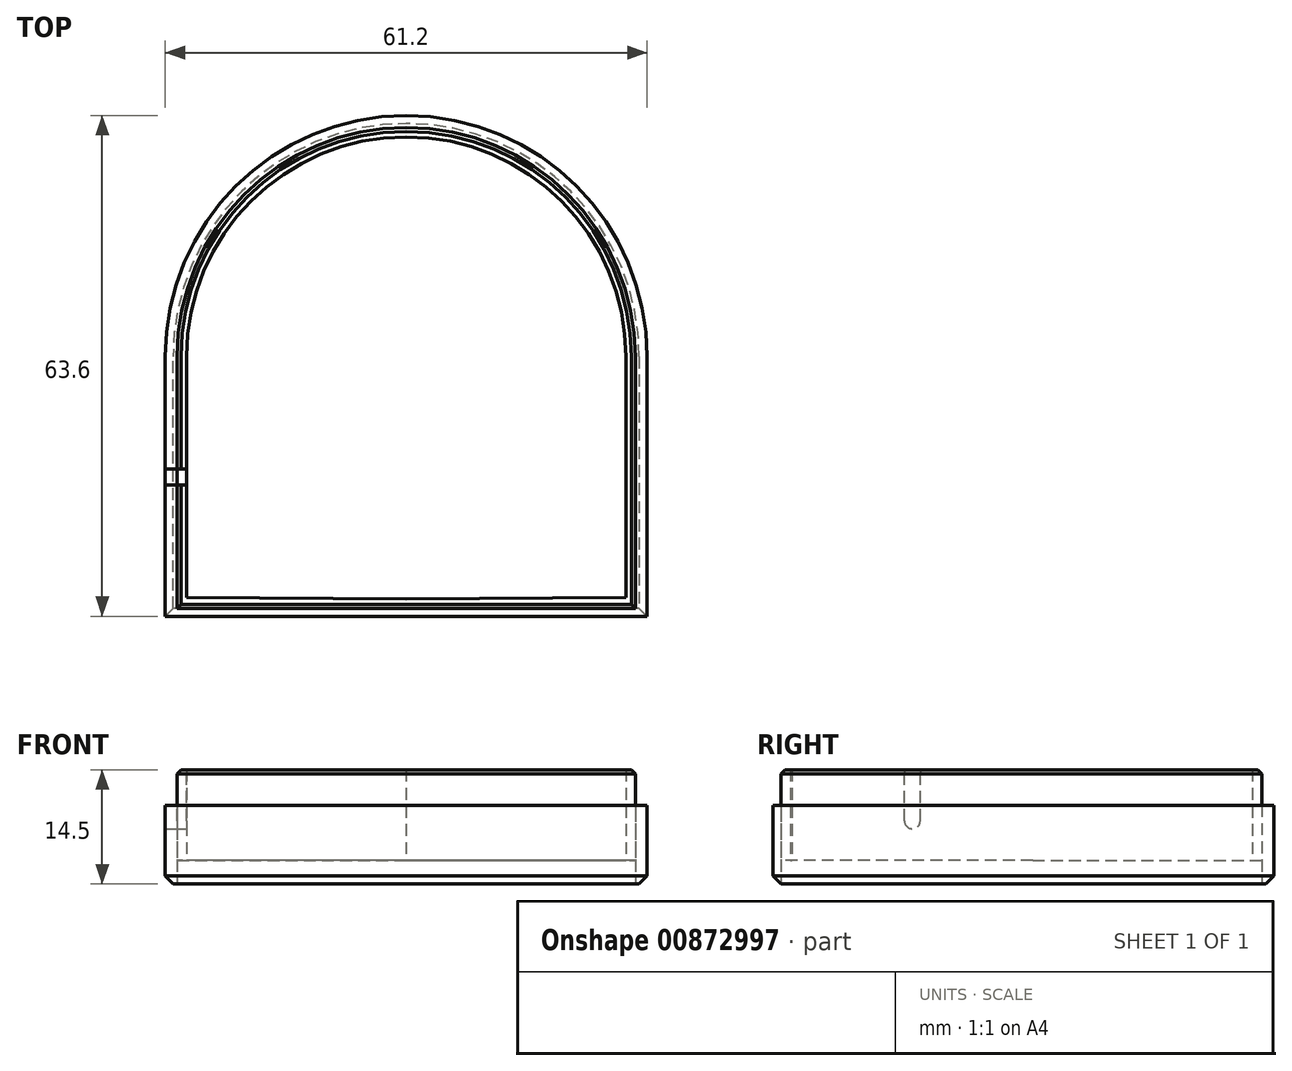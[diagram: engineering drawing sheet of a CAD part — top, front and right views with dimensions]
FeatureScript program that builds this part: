
annotation { "Feature Type Name" : "Feature", "Feature Type Description" : "" }
export const myFeature = defineFeature(function(context is Context, id is Id, definition is map)
    precondition{}
    {
        {
            assignVariable(context, id + "F0", {"name" : "LongExt", "anyValue" : 10});
        }
        {
            assignVariable(context, id + "F1", {"name" : "Renfoncement", "anyValue" : 1.5});
        }
        {
            var Q0;
            Q0=qCreatedBy(makeId("Top.planeOp"),FACE);
            var sketch = newSketch(context, id + "F2", { "sketchPlane" : qUnion([Q0])});
            skCircle(sketch, "E0", {"center": v(0, 0) * mm, "radius": 29.1 * mm});
            skCircle(sketch, "E1", {"center": v(0, 0) * mm, "radius": 30.6 * mm});
            skLineSegment(sketch, "E2", {"start": v(0, 0) * mm, "end": v(0, -33) * mm, "construction": true});
            skLineSegment(sketch, "E3", {"start": v(-30.6, 0) * mm, "end": v(-30.6, -33) * mm});
            skLineSegment(sketch, "E4", {"start": v(30.6, 0) * mm, "end": v(30.6, -33) * mm});
            skLineSegment(sketch, "E5", {"start": v(30.6, -33) * mm, "end": v(-30.6, -33) * mm});
            skLineSegment(sketch, "E6.bottom", {"start": v(0, 0) * mm, "end": v(-24, 0) * mm, "construction": true});
            skLineSegment(sketch, "E7.bottom", {"start": v(0, 0) * mm, "end": v(24, 0) * mm, "construction": true});
            skLineSegment(sketch, "E8.bottom", {"start": v(-29.1, 0) * mm, "end": v(29.1, 0) * mm});
            skLineSegment(sketch, "E8.top", {"start": v(-29.1, -32) * mm, "end": v(29.1, -32) * mm});
            skLineSegment(sketch, "E8.left", {"start": v(-29.1, 0) * mm, "end": v(-29.1, -32) * mm});
            skLineSegment(sketch, "E8.right", {"start": v(29.1, 0) * mm, "end": v(29.1, -32) * mm});
            skSolve(sketch);
        }
        {
            var Q0;
            Q0=makeQuery(id+"F2.imprint","IMPRINT",FACE,{"disambiguationData":[TD([[makeQuery(id+"F2.imprint","IMPRINT",EDGE,{"derivedFrom":sQuery(id+"F2.wireOp",EDGE,"cgQ0b4hG-vElN-mggU-30L2-2sLLd5fgtlCd")}),-1.0]])]});
            var Q1;
            {var subQ0=sQuery(id+"F2.wireOp",EDGE,"E8.left");var subQ6=sQuery(id+"F2.wireOp",EDGE,"E1");var subQ7=makeQuery(id+"F2.imprint","INTERSECT",VERTEX,{"derivedFrom":[subQ6,subQ0]});Q1=makeQuery(id+"F2.imprint","IMPRINT",FACE,{"disambiguationData":[TD([[makeQuery(id+"F2.imprint","IMPRINT",EDGE,{"disambiguationData":[TD([[subQ7,-1.0]])],"derivedFrom":subQ6}),1.0]])]});}
            var Q2;
            {var subQ0=sQuery(id+"F2.wireOp",EDGE,"E8.bottom");var subQ1=sQuery(id+"F2.wireOp",EDGE,"6StlEvJA-1fEL-pRc8-Q0MJ-Zy27nK8FA800");var subQ2=makeQuery(id+"F2.imprint","INTERSECT",VERTEX,{"disambiguationData":[OD(0.0)],"derivedFrom":[subQ1,subQ0]});Q2=makeQuery(id+"F2.imprint","IMPRINT",FACE,{"disambiguationData":[TD([[makeQuery(id+"F2.imprint","IMPRINT",EDGE,{"disambiguationData":[TD([[subQ2,-1.0]])],"derivedFrom":subQ1}),-1.0]])]});}
            var Q3;
            {var subQ0=sQuery(id+"F2.wireOp",EDGE,"E8.bottom");var subQ1=sQuery(id+"F2.wireOp",EDGE,"6StlEvJA-1fEL-pRc8-Q0MJ-Zy27nK8FA800");var subQ2=makeQuery(id+"F2.imprint","INTERSECT",VERTEX,{"disambiguationData":[OD(0.0)],"derivedFrom":[subQ1,subQ0]});Q3=makeQuery(id+"F2.imprint","IMPRINT",FACE,{"disambiguationData":[TD([[makeQuery(id+"F2.imprint","IMPRINT",EDGE,{"disambiguationData":[TD([[subQ2,-1.0]])],"derivedFrom":subQ1}),1.0]])]});}
            var Q4;
            {var subQ0=sQuery(id+"F2.wireOp",EDGE,"E8.bottom");var subQ1=sQuery(id+"F2.wireOp",EDGE,"6StlEvJA-1fEL-pRc8-Q0MJ-Zy27nK8FA800");var subQ2=makeQuery(id+"F2.imprint","INTERSECT",VERTEX,{"disambiguationData":[OD(0.0)],"derivedFrom":[subQ1,subQ0]});Q4=makeQuery(id+"F2.imprint","IMPRINT",FACE,{"disambiguationData":[TD([[makeQuery(id+"F2.imprint","IMPRINT",EDGE,{"disambiguationData":[TD([[subQ2,1.0]])],"derivedFrom":subQ1}),1.0]])]});}
            var Q5;
            {var subQ0=sQuery(id+"F2.wireOp",EDGE,"E8.bottom");var subQ1=sQuery(id+"F2.wireOp",EDGE,"6StlEvJA-1fEL-pRc8-Q0MJ-Zy27nK8FA800");var subQ2=makeQuery(id+"F2.imprint","INTERSECT",VERTEX,{"disambiguationData":[OD(0.0)],"derivedFrom":[subQ1,subQ0]});Q5=makeQuery(id+"F2.imprint","IMPRINT",FACE,{"disambiguationData":[TD([[makeQuery(id+"F2.imprint","IMPRINT",EDGE,{"disambiguationData":[TD([[subQ2,1.0]])],"derivedFrom":subQ1}),-1.0]])]});}
            var Q6;
            {var subQ0=sQuery(id+"F2.wireOp",EDGE,"E8.bottom");Q6=makeQuery(id+"F2.imprint","IMPRINT",FACE,{"disambiguationData":[TD([[makeQuery(id+"F2.imprint","IMPRINT",EDGE,{"derivedFrom":subQ0}),-1.0]])]});}
            var Q7;
            {var subQ0=sQuery(id+"F2.wireOp",EDGE,"E8.bottom");Q7=makeQuery(id+"F2.imprint","IMPRINT",FACE,{"disambiguationData":[TD([[makeQuery(id+"F2.imprint","IMPRINT",EDGE,{"derivedFrom":subQ0}),1.0]])]});}
            var Q8;
            {var subQ5=sQuery(id+"F2.wireOp",EDGE,"E8.top");Q8=makeQuery(id+"F2.imprint","IMPRINT",FACE,{"disambiguationData":[TD([[makeQuery(id+"F2.imprint","IMPRINT",EDGE,{"derivedFrom":subQ5}),1.0]])]});}
            extrude(context, id + "F3", {"entities" : qUnion([Q0, Q1, Q2, Q3, Q4, Q5, Q6, Q7, Q8]), "depth" : 3 * mm, "offsetDistance" : 25 * mm});
        }
        {
            var Q0;
            {var subQ5=sQuery(id+"F2.wireOp",EDGE,"E3");Q0=makeQuery(id+"F2.imprint","IMPRINT",FACE,{"disambiguationData":[TD([[makeQuery(id+"F2.imprint","IMPRINT",EDGE,{"derivedFrom":subQ5}),1.0]])]});}
            var Q1;
            {var subQ0=sQuery(id+"F2.wireOp",EDGE,"E1");var subQ1=makeQuery(id+"F2.imprint","INTERSECT",VERTEX,{"derivedFrom":[subQ0,sQuery(id+"F2.wireOp",EDGE,"E3")]});Q1=makeQuery(id+"F2.imprint","IMPRINT",FACE,{"disambiguationData":[TD([[makeQuery(id+"F2.imprint","IMPRINT",EDGE,{"disambiguationData":[TD([[subQ1,1.0]])],"derivedFrom":subQ0}),1.0]])]});}
            extrude(context, id + "F4", {"entities" : qUnion([Q0, Q1]), "depth" : (getVariable(context, 'LongExt')) * mm, "offsetDistance" : 25 * mm});
        }
        {
            var Q0;
            Q0=makeQuery(id+"F4.opExtrude","CAP_EDGE",EDGE,{"disambiguationData":[OSD([sQuery(id+"F2.wireOp",EDGE,"E4")])],"isStart":true});
            var Q1;
            Q1=makeQuery(id+"F4.opExtrude","CAP_EDGE",EDGE,{"disambiguationData":[OSD([sQuery(id+"F2.wireOp",EDGE,"E5")])],"isStart":true});
            var Q2;
            Q2=makeQuery(id+"F4.opExtrude","CAP_EDGE",EDGE,{"disambiguationData":[OSD([sQuery(id+"F2.wireOp",EDGE,"E3")])],"isStart":true});
            var Q3;
            Q3=makeQuery(id+"F4.opExtrude","CAP_EDGE",EDGE,{"disambiguationData":[OSD([sQuery(id+"F2.wireOp",EDGE,"E1")])],"isStart":true});
            chamfer(context, id + "F5", {"entities" : qUnion([Q0, Q1, Q2, Q3]), "width" : 1 * mm, "tangentPropagation" : true});
        }
        {
            var Q0;
            Q0=makeQuery(id+"F3.opExtrude","CAP_FACE",FACE,{"disambiguationData":[OSD([sQuery(id+"F2.wireOp",EDGE,"E0"),sQuery(id+"F2.wireOp",EDGE,"E8.top"),sQuery(id+"F2.wireOp",EDGE,"E8.left"),sQuery(id+"F2.wireOp",EDGE,"E8.right")])],"isStart":false});
            var sketch = newSketch(context, id + "F6", { "sketchPlane" : qUnion([Q0])});
            skCircle(sketch, "E9", {"center": v(0, 0) * mm, "radius": 27.9 * mm});
            skLineSegment(sketch, "E10", {"start": v(0, 0) * mm, "end": v(-27.9, 0) * mm, "construction": true});
            skLineSegment(sketch, "E11", {"start": v(-27.9, 0) * mm, "end": v(-27.9, -30.6) * mm, "construction": true});
            skLineSegment(sketch, "E12", {"start": v(0, 0) * mm, "end": v(0, -30.8) * mm, "construction": true});
            skLineSegment(sketch, "E13", {"start": v(-27.9, 0) * mm, "end": v(-27.9, -30.6) * mm});
            skLineSegment(sketch, "E14", {"start": v(0, -30.8) * mm, "end": v(-27.9, -30.6) * mm});
            skLineSegment(sketch, "E15.MirrorCS", {"start": v(27.9, 0) * mm, "end": v(27.9, -30.6) * mm, "construction": true});
            skLineSegment(sketch, "E16.MirrorCS", {"start": v(0, -30.8) * mm, "end": v(27.9, -30.6) * mm});
            skLineSegment(sketch, "E17", {"start": v(27.9, 0) * mm, "end": v(27.9, -30.6) * mm});
            skSolve(sketch);
        }
        {
            assignVariable(context, id + "F7", {"name" : "LongRenf", "anyValue" : getVariable(context, 'LongExt') + getVariable(context, 'Renfoncement')});
        }
        {
            var Q0;
            {var subQ0=sQuery(id+"F6.wireOp",EDGE,"E13");Q0=makeQuery(id+"F6.imprint","IMPRINT",FACE,{"disambiguationData":[TD([[makeQuery(id+"F6.imprint","IMPRINT",EDGE,{"derivedFrom":subQ0}),-1.0]])]});}
            extrude(context, id + "F8", {"entities" : qUnion([Q0]), "depth" : (getVariable(context, 'LongRenf')) * mm, "offsetDistance" : 25 * mm});
        }
        {
            var Q0;
            Q0=makeQuery(id+"F8.opExtrude","CAP_EDGE",EDGE,{"disambiguationData":[OSD([sQuery(id+"F2.wireOp",EDGE,"E8.left")])],"isStart":false});
            var Q1;
            Q1=makeQuery(id+"F8.opExtrude","CAP_EDGE",EDGE,{"disambiguationData":[OSD([sQuery(id+"F2.wireOp",EDGE,"E0")])],"isStart":false});
            var Q2;
            Q2=makeQuery(id+"F8.opExtrude","CAP_EDGE",EDGE,{"disambiguationData":[OSD([sQuery(id+"F2.wireOp",EDGE,"E8.right")])],"isStart":false});
            var Q3;
            Q3=makeQuery(id+"F8.opExtrude","CAP_EDGE",EDGE,{"disambiguationData":[OSD([sQuery(id+"F2.wireOp",EDGE,"E8.top")])],"isStart":false});
            chamfer(context, id + "F9", {"entities" : qUnion([Q0, Q1, Q2, Q3]), "width" : 0.5 * mm, "tangentPropagation" : true});
        }
        {
            var Q0;
            Q0=makeQuery(id+"F8.opExtrude","SWEPT_FACE",FACE,{"disambiguationData":[OSD([sQuery(id+"F6.wireOp",EDGE,"E13")])]});
            var sketch = newSketch(context, id + "F10", { "sketchPlane" : qUnion([Q0])});
            skLineSegment(sketch, "E18", {"start": v(-15.3, 14.5) * mm, "end": v(0, 14.5) * mm, "construction": true});
            skLineSegment(sketch, "E19", {"start": v(-15.3, 14.5) * mm, "end": v(-15.3, 8) * mm, "construction": true});
            skCircle(sketch, "E20", {"center": v(-15.3, 8) * mm, "radius": 1 * mm});
            skLineSegment(sketch, "E21", {"start": v(-15.3, 8) * mm, "end": v(-16.3, 8) * mm, "construction": true});
            skLineSegment(sketch, "E22", {"start": v(-16.3, 8) * mm, "end": v(-14.3, 8) * mm, "construction": true});
            skLineSegment(sketch, "E23", {"start": v(-16.3, 8) * mm, "end": v(-16.3, 14.5) * mm});
            skLineSegment(sketch, "E24.MirrorCS", {"start": v(-14.3, 8) * mm, "end": v(-14.3, 14.5) * mm});
            skSolve(sketch);
        }
        {
            var Q0;
            {var subQ0=sQuery(id+"F10.wireOp",EDGE,"E20");var subQ1=makeQuery(id+"F10.imprint","INTERSECT",VERTEX,{"derivedFrom":[subQ0,sQuery(id+"F10.wireOp",EDGE,"E23")]});Q0=makeQuery(id+"F10.imprint","IMPRINT",FACE,{"disambiguationData":[TD([[makeQuery(id+"F10.imprint","IMPRINT",EDGE,{"disambiguationData":[TD([[subQ1,1.0]])],"derivedFrom":subQ0}),1.0]])]});}
            var Q1;
            {var subQ0=sQuery(id+"F10.wireOp",EDGE,"E23");Q1=makeQuery(id+"F10.imprint","IMPRINT",FACE,{"disambiguationData":[TD([[makeQuery(id+"F10.imprint","IMPRINT",EDGE,{"derivedFrom":subQ0}),-1.0]])]});}
            extrude(context, id + "F11", {"entities" : qUnion([Q0, Q1]), "operationType" : NewBodyOperationType.REMOVE, "oppositeDirection" : true, "depth" : 25 * mm, "offsetDistance" : 25 * mm});
        }
        {
            var Q0;
            Q0=makeQuery(id+"F4.opExtrude","SWEPT_FACE",FACE,{"disambiguationData":[OSD([sQuery(id+"F2.wireOp",EDGE,"E8.left")])]});
            var sketch = newSketch(context, id + "F12", { "sketchPlane" : qUnion([Q0])});
            skLineSegment(sketch, "E25", {"start": v(0, 10) * mm, "end": v(-15.3, 10) * mm, "construction": true});
            skLineSegment(sketch, "E26", {"start": v(-15.3, 10) * mm, "end": v(-15.3, 8) * mm, "construction": true});
            skCircle(sketch, "E27", {"center": v(-15.3, 8) * mm, "radius": 1 * mm});
            skLineSegment(sketch, "E28", {"start": v(-15.3, 8) * mm, "end": v(-14.3, 8) * mm});
            skLineSegment(sketch, "E29", {"start": v(-14.3, 8) * mm, "end": v(-14.3, 10) * mm});
            skLineSegment(sketch, "E30", {"start": v(-16.3, 8) * mm, "end": v(-16.3, 10) * mm});
            skSolve(sketch);
        }
        {
            var Q0;
            {var subQ0=sQuery(id+"F12.wireOp",EDGE,"E29");Q0=makeQuery(id+"F12.imprint","IMPRINT",FACE,{"disambiguationData":[TD([[makeQuery(id+"F12.imprint","IMPRINT",EDGE,{"derivedFrom":subQ0}),1.0]])]});}
            var Q1;
            {var subQ0=sQuery(id+"F12.wireOp",EDGE,"E27");var subQ1=makeQuery(id+"F12.imprint","INTERSECT",VERTEX,{"derivedFrom":[subQ0,sQuery(id+"F12.wireOp",EDGE,"E29")]});Q1=makeQuery(id+"F12.imprint","IMPRINT",FACE,{"disambiguationData":[TD([[makeQuery(id+"F12.imprint","IMPRINT",EDGE,{"disambiguationData":[TD([[subQ1,-1.0]])],"derivedFrom":subQ0}),1.0]])]});}
            extrude(context, id + "F13", {"entities" : qUnion([Q0, Q1]), "operationType" : NewBodyOperationType.REMOVE, "oppositeDirection" : true, "depth" : 25 * mm, "offsetDistance" : 25 * mm});
        }
    });
